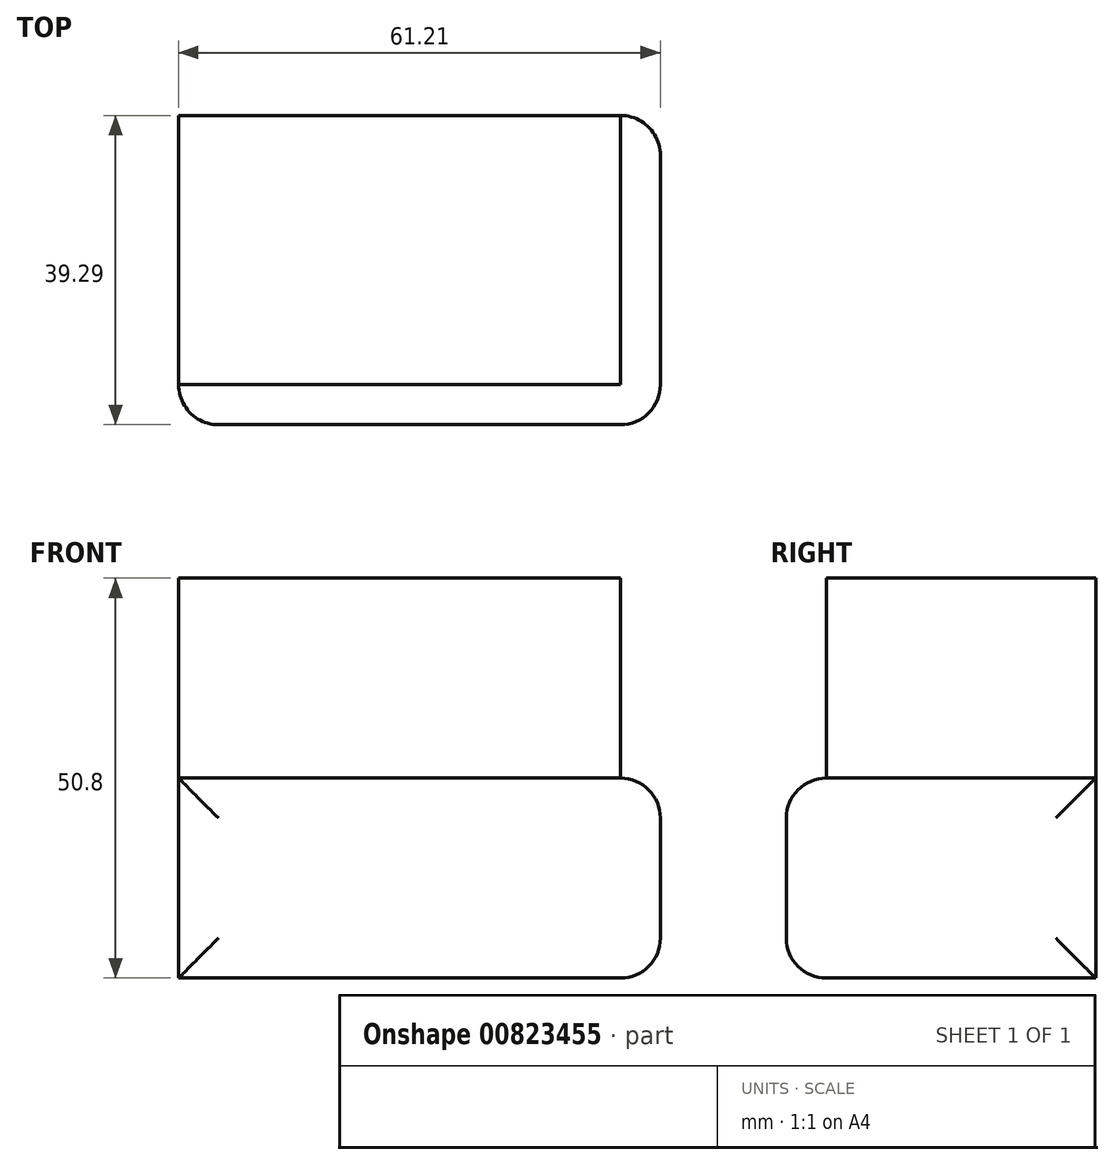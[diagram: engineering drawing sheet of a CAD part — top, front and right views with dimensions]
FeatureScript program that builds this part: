
annotation { "Feature Type Name" : "Feature", "Feature Type Description" : "" }
export const myFeature = defineFeature(function(context is Context, id is Id, definition is map)
    precondition{}
    {
        {
            var Q0;
            Q0=qCreatedBy(makeId("Top.planeOp"),FACE);
            var sketch = newSketch(context, id + "F0", { "sketchPlane" : qUnion([Q0])});
            skLineSegment(sketch, "E0.bottom", {"start": v(0, 0) * mm, "end": v(61.21, 0) * mm});
            skLineSegment(sketch, "E0.top", {"start": v(0, 39.29) * mm, "end": v(61.21, 39.29) * mm});
            skLineSegment(sketch, "E0.left", {"start": v(0, 0) * mm, "end": v(0, 39.29) * mm});
            skLineSegment(sketch, "E0.right", {"start": v(61.21, 0) * mm, "end": v(61.21, 39.29) * mm});
            skLineSegment(sketch, "E1.bottom", {"start": v(61.21, 39.29) * mm, "end": v(-30.03, 39.29) * mm});
            skLineSegment(sketch, "E1.top", {"start": v(61.21, -22.86) * mm, "end": v(-30.03, -22.86) * mm});
            skLineSegment(sketch, "E1.left", {"start": v(61.21, 39.29) * mm, "end": v(61.21, -22.86) * mm});
            skLineSegment(sketch, "E1.right", {"start": v(-30.03, 39.29) * mm, "end": v(-30.03, -22.86) * mm});
            skSolve(sketch);
        }
        {
            var Q0;
            Q0=makeQuery(id+"F0.imprint","IMPRINT",FACE,{"disambiguationData":[TD([[makeQuery(id+"F0.imprint","IMPRINT",EDGE,{"derivedFrom":sQuery(id+"F0.wireOp",EDGE,"E0.bottom")}),1.0]])]});
            extrude(context, id + "F1", {"entities" : qUnion([Q0]), "depth" : 25.4 * mm, "offsetDistance" : 25.4 * mm});
        }
        {
            var Q0;
            Q0=makeQuery(id+"F1.opExtrude","SWEPT_FACE",FACE,{"disambiguationData":[OSD([sQuery(id+"F0.wireOp",EDGE,"E0.bottom")])]});
            var Q1;
            Q1=makeQuery(id+"F1.opExtrude","CAP_EDGE",EDGE,{"disambiguationData":[OSD([sQuery(id+"F0.wireOp",EDGE,"E0.right")])],"isStart":false});
            var Q2;
            Q2=makeQuery(id+"F1.opExtrude","SWEPT_FACE",FACE,{"disambiguationData":[OSD([sQuery(id+"F0.wireOp",EDGE,"E0.right")])]});
            fillet(context, id + "F2", {"entities" : qUnion([Q0, Q1, Q2]), "radius" : 5.08 * mm, "tangentPropagation" : true, "allowEdgeOverflow" : false});
        }
        {
            var Q0;
            Q0=makeQuery(id+"F1.opExtrude","CAP_FACE",FACE,{"disambiguationData":[OSD([sQuery(id+"F0.wireOp",EDGE,"E0.bottom"),sQuery(id+"F0.wireOp",EDGE,"E0.top"),sQuery(id+"F0.wireOp",EDGE,"E0.left"),sQuery(id+"F0.wireOp",EDGE,"E0.right")])],"isStart":false});
            extrude(context, id + "F3", {"entities" : qUnion([Q0]), "operationType" : NewBodyOperationType.ADD, "depth" : 25.4 * mm, "offsetDistance" : 25.4 * mm});
        }
    });
